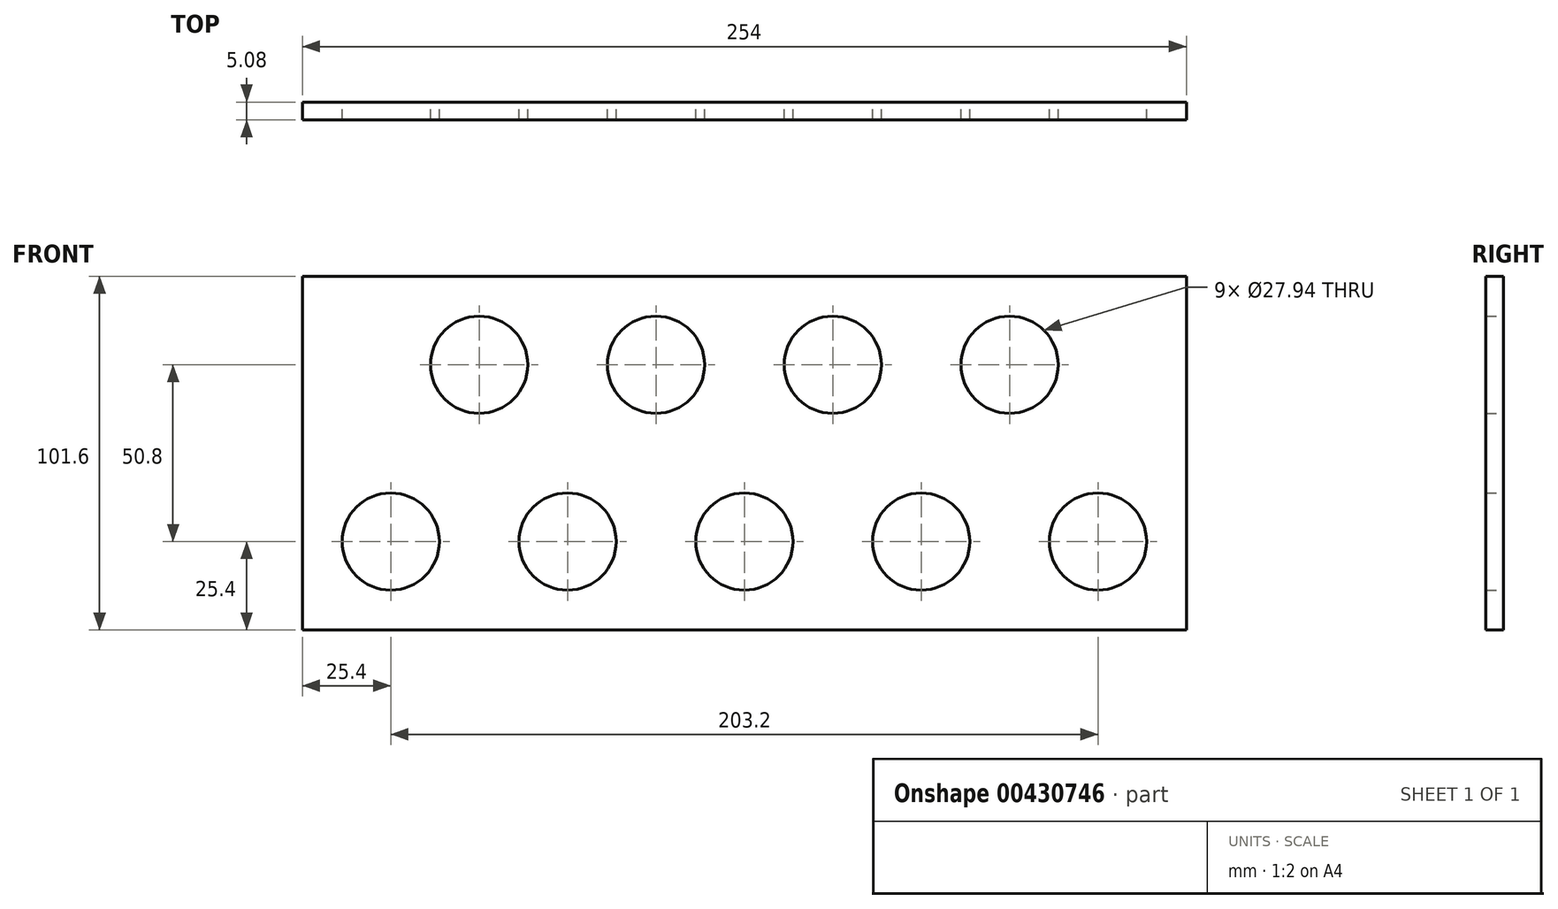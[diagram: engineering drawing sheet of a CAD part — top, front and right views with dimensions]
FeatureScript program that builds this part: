
annotation { "Feature Type Name" : "Feature", "Feature Type Description" : "" }
export const myFeature = defineFeature(function(context is Context, id is Id, definition is map)
    precondition{}
    {
        {
            var Q0;
            Q0=qCreatedBy(makeId("Front.planeOp"),FACE);
            var sketch = newSketch(context, id + "F0", { "sketchPlane" : qUnion([Q0])});
            skLineSegment(sketch, "E0.bottom", {"start": v(0, 0) * mm, "end": v(254, 0) * mm});
            skLineSegment(sketch, "E0.top", {"start": v(0, 101.6) * mm, "end": v(254, 101.6) * mm});
            skLineSegment(sketch, "E0.left", {"start": v(0, 0) * mm, "end": v(0, 101.6) * mm});
            skLineSegment(sketch, "E0.right", {"start": v(254, 0) * mm, "end": v(254, 101.6) * mm});
            skCircle(sketch, "E1", {"center": v(25.4, 25.4) * mm, "radius": 13.97 * mm});
            skCircle(sketch, "E2.1.0.0", {"center": v(76.2, 25.4) * mm, "radius": 13.97 * mm});
            skCircle(sketch, "E2.2.0.0", {"center": v(127, 25.4) * mm, "radius": 13.97 * mm});
            skCircle(sketch, "E2.3.0.0", {"center": v(177.8, 25.4) * mm, "radius": 13.97 * mm});
            skCircle(sketch, "E2.4.0.0", {"center": v(228.6, 25.4) * mm, "radius": 13.97 * mm});
            skLineSegment(sketch, "E2.direction1", {"start": v(25.4, 25.4) * mm, "end": v(76.2, 25.4) * mm, "construction": true});
            skCircle(sketch, "E3", {"center": v(50.8, 76.2) * mm, "radius": 13.97 * mm});
            skLineSegment(sketch, "E4", {"start": v(50.8, 25.4) * mm, "end": v(50.8, 76.2) * mm, "construction": true});
            skCircle(sketch, "E5.1.0.0", {"center": v(101.6, 76.2) * mm, "radius": 13.97 * mm});
            skCircle(sketch, "E5.2.0.0", {"center": v(152.4, 76.2) * mm, "radius": 13.97 * mm});
            skCircle(sketch, "E5.3.0.0", {"center": v(203.2, 76.2) * mm, "radius": 13.97 * mm});
            skLineSegment(sketch, "E5.direction1", {"start": v(50.8, 76.2) * mm, "end": v(101.6, 76.2) * mm, "construction": true});
            skLineSegment(sketch, "E6.bottom", {"start": v(0, 0) * mm, "end": v(25.4, 0) * mm, "construction": true});
            skLineSegment(sketch, "E6.top", {"start": v(0, 25.4) * mm, "end": v(25.4, 25.4) * mm, "construction": true});
            skLineSegment(sketch, "E6.left", {"start": v(0, 0) * mm, "end": v(0, 25.4) * mm, "construction": true});
            skLineSegment(sketch, "E6.right", {"start": v(25.4, 0) * mm, "end": v(25.4, 25.4) * mm, "construction": true});
            skSolve(sketch);
        }
        {
            var Q0;
            Q0=makeQuery(id+"F0.imprint","IMPRINT",FACE,{"disambiguationData":[TD([[makeQuery(id+"F0.imprint","IMPRINT",EDGE,{"derivedFrom":sQuery(id+"F0.wireOp",EDGE,"E0.bottom")}),1.0]])]});
            extrude(context, id + "F1", {"entities" : qUnion([Q0]), "depth" : 5.08 * mm});
        }
    });
